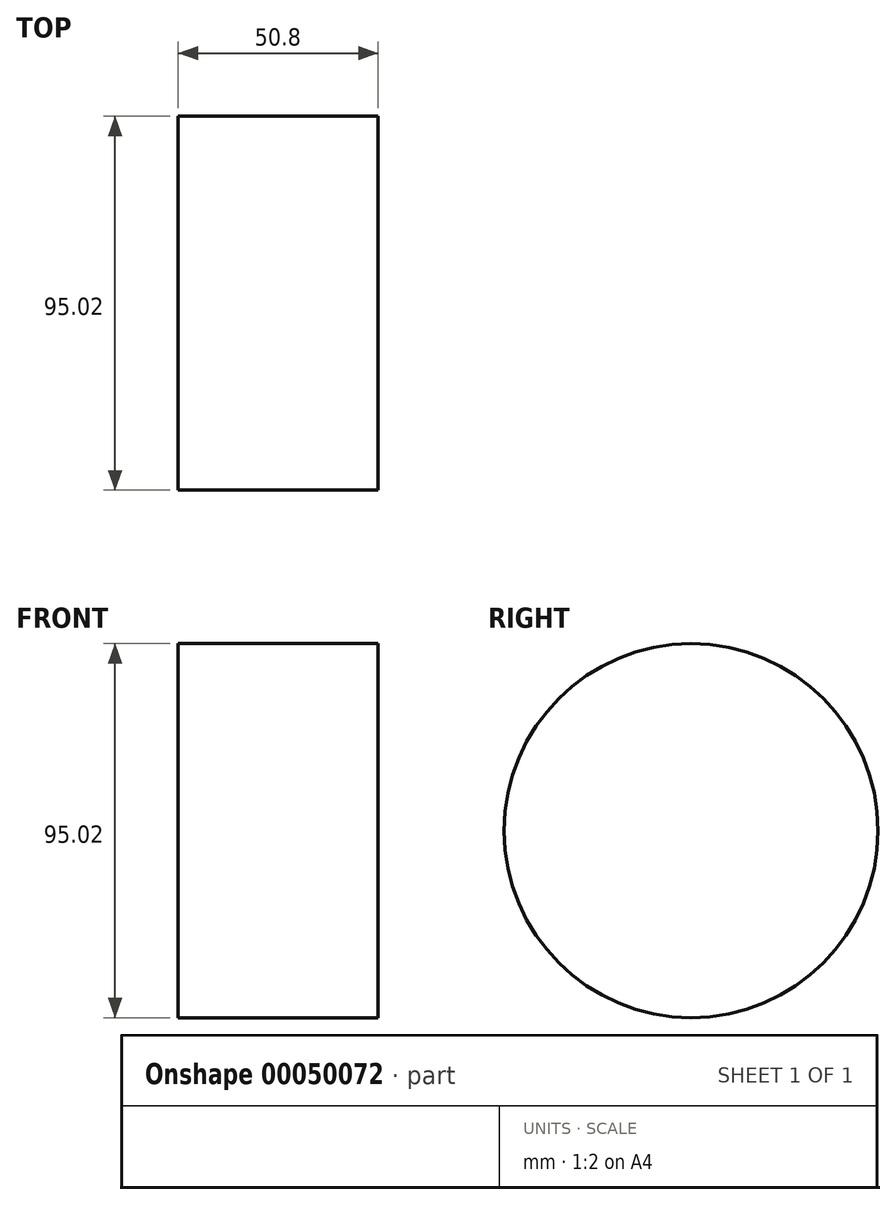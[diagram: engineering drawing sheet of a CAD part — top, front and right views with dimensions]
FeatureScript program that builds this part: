
annotation { "Feature Type Name" : "Feature", "Feature Type Description" : "" }
export const myFeature = defineFeature(function(context is Context, id is Id, definition is map)
    precondition{}
    {
        {
            var Q0;
            Q0=qCreatedBy(makeId("Right.planeOp"),FACE);
            var sketch = newSketch(context, id + "F0", { "sketchPlane" : qUnion([Q0])});
            skCircle(sketch, "E0", {"center": v(0, 0) * mm, "radius": 47.5 * mm});
            skSolve(sketch);
        }
        {
            var Q0;
            Q0=sQuery(id+"F0.wireOp",EDGE,"E0");
            extrude(context, id + "F1", {"bodyType" : ToolBodyType.SURFACE, "surfaceEntities" : qUnion([Q0]), "depth" : 50.8 * mm});
        }
    });
